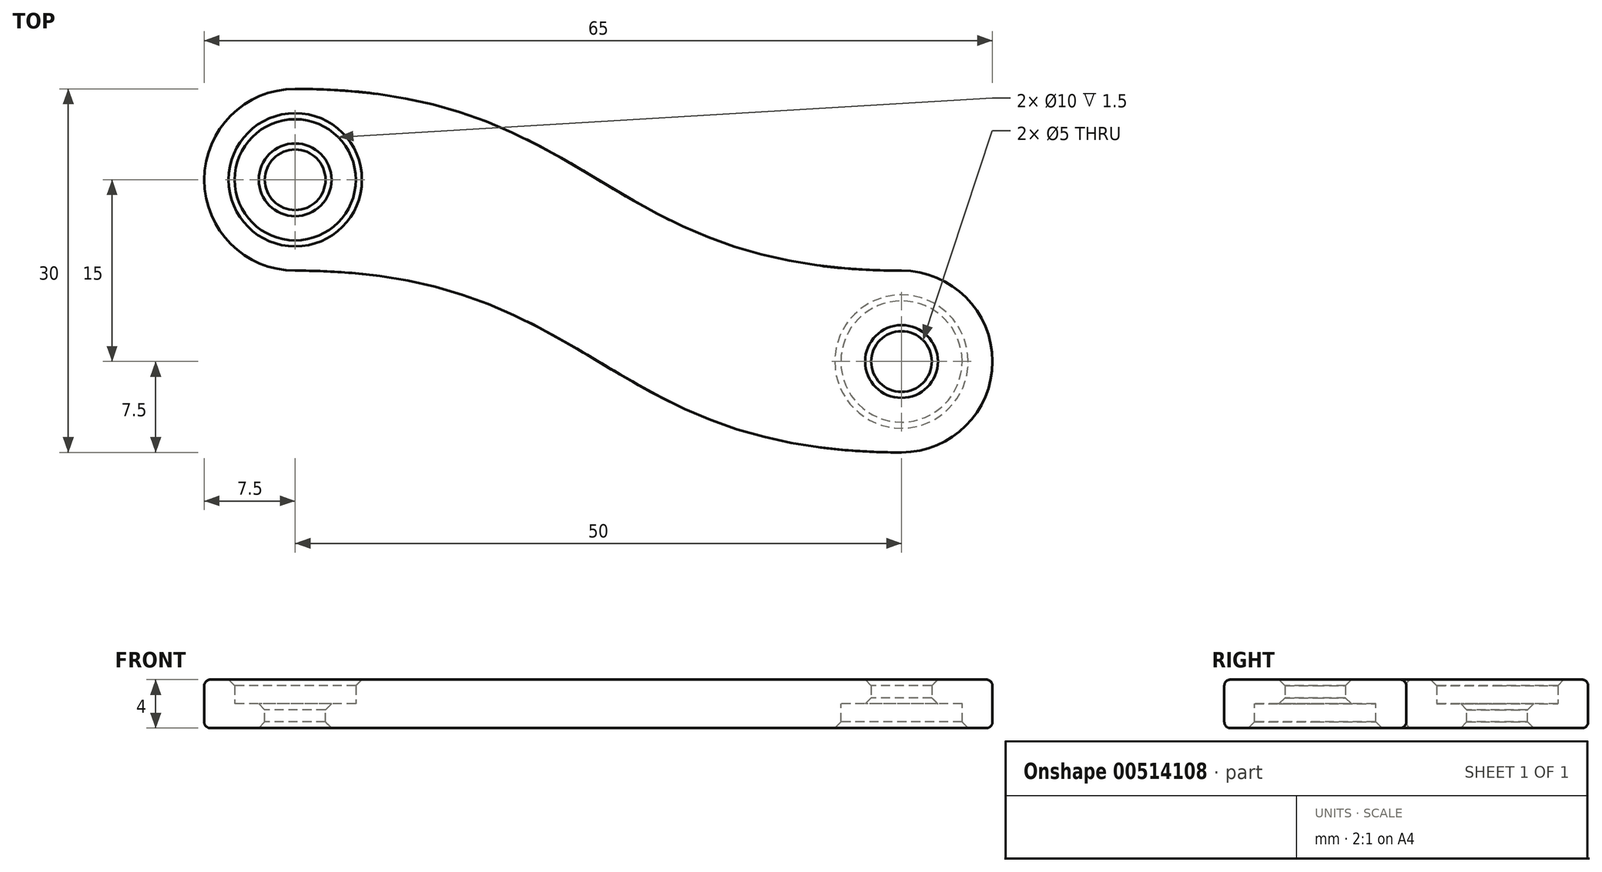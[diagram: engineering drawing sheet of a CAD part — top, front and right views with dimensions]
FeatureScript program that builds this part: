
annotation { "Feature Type Name" : "Feature", "Feature Type Description" : "" }
export const myFeature = defineFeature(function(context is Context, id is Id, definition is map)
    precondition{}
    {
        {
            var Q0;
            Q0=qCreatedBy(makeId("Top.planeOp"),FACE);
            var sketch = newSketch(context, id + "F0", { "sketchPlane" : qUnion([Q0])});
            skCircle(sketch, "E0", {"center": v(-25, 7.5) * mm, "radius": 7.5 * mm});
            skCircle(sketch, "E1", {"center": v(25, -7.5) * mm, "radius": 7.5 * mm});
            skFitSpline(sketch, "E2", {"points": [v(-25, 15) * mm, v(25, 0) * mm], "startDerivative": vector(75, 0) * mm, "endDerivative": vector(75, 0) * mm});
            skFitSpline(sketch, "E3", {"points": [v(-25, 0) * mm, v(25, -15) * mm], "startDerivative": vector(75, 0) * mm, "endDerivative": vector(75, 0) * mm});
            skCircle(sketch, "E4", {"center": v(-25, 7.5) * mm, "radius": 5 * mm});
            skCircle(sketch, "E5", {"center": v(-25, 7.5) * mm, "radius": 2.5 * mm});
            skCircle(sketch, "E6", {"center": v(25, -7.5) * mm, "radius": 5 * mm});
            skCircle(sketch, "E7", {"center": v(25, -7.5) * mm, "radius": 2.5 * mm});
            skSolve(sketch);
        }
        {
            var Q0;
            Q0=makeQuery(id+"F0.imprint","IMPRINT",FACE,{"disambiguationData":[TD([[makeQuery(id+"F0.imprint","IMPRINT",EDGE,{"derivedFrom":sQuery(id+"F0.wireOp",EDGE,"E4")}),-1.0]])]});
            var Q1;
            {var subQ0=sQuery(id+"F0.wireOp",EDGE,"E2");Q1=makeQuery(id+"F0.imprint","IMPRINT",FACE,{"disambiguationData":[TD([[makeQuery(id+"F0.imprint","IMPRINT",EDGE,{"derivedFrom":subQ0}),-1.0]])]});}
            var Q2;
            Q2=makeQuery(id+"F0.imprint","IMPRINT",FACE,{"disambiguationData":[TD([[makeQuery(id+"F0.imprint","IMPRINT",EDGE,{"derivedFrom":sQuery(id+"F0.wireOp",EDGE,"E6")}),1.0]])]});
            var Q3;
            Q3=makeQuery(id+"F0.imprint","IMPRINT",FACE,{"disambiguationData":[TD([[makeQuery(id+"F0.imprint","IMPRINT",EDGE,{"derivedFrom":sQuery(id+"F0.wireOp",EDGE,"E6")}),-1.0]])]});
            extrude(context, id + "F1", {"entities" : qUnion([Q0, Q1, Q2, Q3]), "depth" : 2 * mm, "offsetDistance" : 25 * mm});
        }
        {
            var Q0;
            Q0=makeQuery(id+"F0.imprint","IMPRINT",FACE,{"disambiguationData":[TD([[makeQuery(id+"F0.imprint","IMPRINT",EDGE,{"derivedFrom":sQuery(id+"F0.wireOp",EDGE,"E4")}),-1.0]])]});
            var Q1;
            {var subQ0=sQuery(id+"F0.wireOp",EDGE,"E2");Q1=makeQuery(id+"F0.imprint","IMPRINT",FACE,{"disambiguationData":[TD([[makeQuery(id+"F0.imprint","IMPRINT",EDGE,{"derivedFrom":subQ0}),-1.0]])]});}
            var Q2;
            Q2=makeQuery(id+"F0.imprint","IMPRINT",FACE,{"disambiguationData":[TD([[makeQuery(id+"F0.imprint","IMPRINT",EDGE,{"derivedFrom":sQuery(id+"F0.wireOp",EDGE,"E6")}),-1.0]])]});
            var Q3;
            Q3=makeQuery(id+"F0.imprint","IMPRINT",FACE,{"disambiguationData":[TD([[makeQuery(id+"F0.imprint","IMPRINT",EDGE,{"derivedFrom":sQuery(id+"F0.wireOp",EDGE,"E4")}),1.0]])]});
            extrude(context, id + "F2", {"entities" : qUnion([Q0, Q1, Q2, Q3]), "operationType" : NewBodyOperationType.ADD, "depth" : -2 * mm, "offsetDistance" : 25 * mm});
        }
        {
            var Q0;
            Q0=makeQuery(id+"F1.opExtrude","CAP_EDGE",EDGE,{"disambiguationData":[OSD([sQuery(id+"F0.wireOp",EDGE,"E4")])],"isStart":false});
            var Q1;
            Q1=makeQuery(id+"F1.opExtrude","CAP_EDGE",EDGE,{"disambiguationData":[OSD([sQuery(id+"F0.wireOp",EDGE,"E7")])],"isStart":false});
            var Q2;
            Q2=makeQuery(id+"F2.opExtrude","CAP_EDGE",EDGE,{"disambiguationData":[OSD([sQuery(id+"F0.wireOp",EDGE,"E5")])],"isStart":true});
            var Q3;
            Q3=makeQuery(id+"F2.opExtrude","CAP_EDGE",EDGE,{"disambiguationData":[OSD([sQuery(id+"F0.wireOp",EDGE,"E5")])],"isStart":false});
            var Q4;
            Q4=makeQuery(id+"F2.opExtrude","CAP_EDGE",EDGE,{"disambiguationData":[OSD([sQuery(id+"F0.wireOp",EDGE,"E6")])],"isStart":false});
            var Q5;
            Q5=makeQuery(id+"F1.opExtrude","CAP_EDGE",EDGE,{"disambiguationData":[OSD([sQuery(id+"F0.wireOp",EDGE,"E7")])],"isStart":true});
            chamfer(context, id + "F3", {"entities" : qUnion([Q0, Q1, Q2, Q3, Q4, Q5]), "width" : 0.5 * mm, "tangentPropagation" : true});
        }
        {
            var Q0;
            Q0=makeQuery(id+"F2.opExtrude","CAP_EDGE",EDGE,{"disambiguationData":[OSD([sQuery(id+"F0.wireOp",EDGE,"E2")])],"isStart":false});
            var Q1;
            Q1=makeQuery(id+"F1.opExtrude","CAP_EDGE",EDGE,{"disambiguationData":[OSD([sQuery(id+"F0.wireOp",EDGE,"E2")])],"isStart":false});
            fillet(context, id + "F4", {"entities" : qUnion([Q0, Q1]), "radius" : 0.5 * mm, "tangentPropagation" : true, "allowEdgeOverflow" : false});
        }
    });
